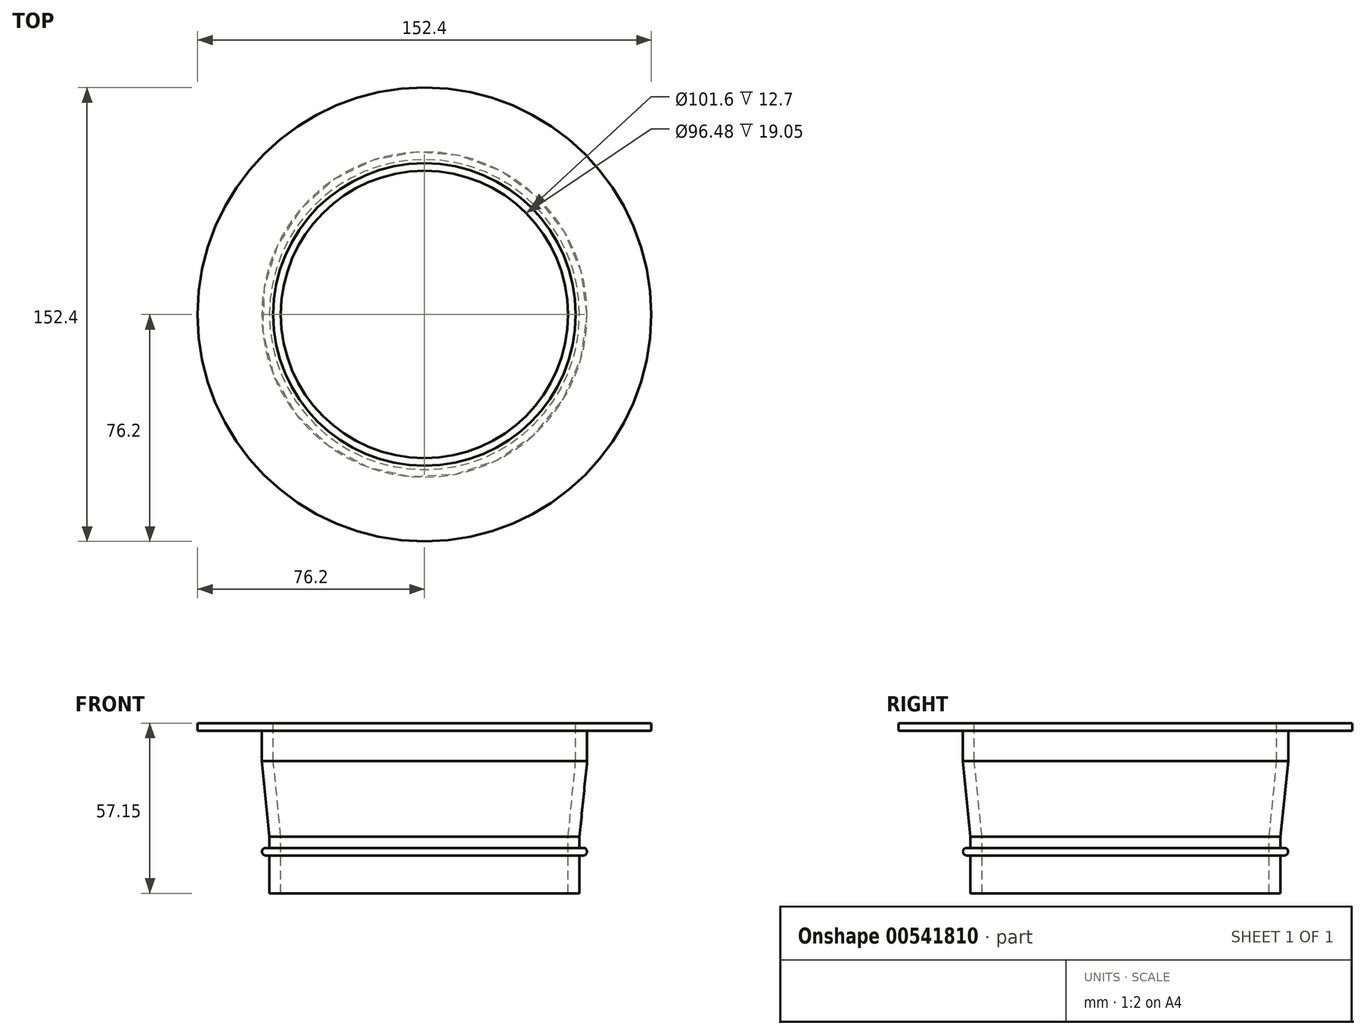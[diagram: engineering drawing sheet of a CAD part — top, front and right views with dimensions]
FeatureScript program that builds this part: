
annotation { "Feature Type Name" : "Feature", "Feature Type Description" : "" }
export const myFeature = defineFeature(function(context is Context, id is Id, definition is map)
    precondition{}
    {
        {
            var Q0;
            Q0=qCreatedBy(makeId("Right.planeOp"),FACE);
            var sketch = newSketch(context, id + "F0", { "sketchPlane" : qUnion([Q0])});
            skLineSegment(sketch, "E0", {"start": v(-48.24, 0) * mm, "end": v(-50.8, 25.4) * mm});
            skLineSegment(sketch, "E1", {"start": v(-52.07, 0) * mm, "end": v(-54.63, 25.4) * mm});
            skLineSegment(sketch, "E2", {"start": v(-54.63, 25.4) * mm, "end": v(-54.63, 38.1) * mm});
            skLineSegment(sketch, "E3", {"start": v(-50.8, 25.4) * mm, "end": v(-50.8, 38.1) * mm});
            skLineSegment(sketch, "E4", {"start": v(-50.8, 38.1) * mm, "end": v(-54.63, 38.1) * mm});
            skLineSegment(sketch, "E5", {"start": v(-48.24, 0) * mm, "end": v(-48.24, -19.05) * mm});
            skLineSegment(sketch, "E6", {"start": v(-52.07, 0) * mm, "end": v(-52.07, -3.81) * mm});
            skLineSegment(sketch, "E7", {"start": v(-48.24, -19.05) * mm, "end": v(-52.07, -19.05) * mm});
            skLineSegment(sketch, "E8", {"start": v(0, 59.15) * mm, "end": v(0, -21.14) * mm});
            skLineSegment(sketch, "E9", {"start": v(-52.07, -3.81) * mm, "end": v(-54.6, -3.81) * mm});
            skLineSegment(sketch, "E10", {"start": v(-54.6, -3.81) * mm, "end": v(-54.6, -6.35) * mm});
            skLineSegment(sketch, "E11", {"start": v(-54.6, -6.35) * mm, "end": v(-52.07, -6.35) * mm});
            skLineSegment(sketch, "E12.trimOffspring", {"start": v(-52.07, -6.35) * mm, "end": v(-52.07, -19.05) * mm});
            skSolve(sketch);
        }
        {
            var Q0;
            Q0=makeQuery(id+"F0.imprint","IMPRINT",FACE,{"disambiguationData":[TD([[makeQuery(id+"F0.imprint","IMPRINT",EDGE,{"derivedFrom":sQuery(id+"F0.wireOp",EDGE,"E0")}),1.0]])]});
            var Q1;
            Q1=sQuery(id+"F0.wireOp",EDGE,"E8");
            revolve(context, id + "F1", {"entities" : qUnion([Q0]), "axis" : qUnion([Q1]), "revolveType" : RevolveType.FULL});
        }
        {
            var Q0;
            Q0=makeQuery(id+"F1.opRevolve","SWEPT_FACE",FACE,{"disambiguationData":[OSD([sQuery(id+"F0.wireOp",EDGE,"E4")])]});
            var sketch = newSketch(context, id + "F2", { "sketchPlane" : qUnion([Q0])});
            skCircle(sketch, "E13", {"center": v(0, 0) * mm, "radius": 76.2 * mm});
            skCircle(sketch, "E14", {"center": v(0, 0) * mm, "radius": 52.1 * mm});
            skSolve(sketch);
        }
        {
            var Q0;
            Q0=makeQuery(id+"F2.imprint","IMPRINT",FACE,{"disambiguationData":[TD([[makeQuery(id+"F2.imprint","IMPRINT",EDGE,{"derivedFrom":sQuery(id+"F2.wireOp",EDGE,"E13")}),1.0]])]});
            var Q1;
            Q1=makeQuery(id+"F2.imprint","IMPRINT",FACE,{"disambiguationData":[TD([[makeQuery(id+"F2.imprint","IMPRINT",EDGE,{"derivedFrom":sQuery(id+"F2.wireOp",EDGE,"E14")}),-1.0]])]});
            extrude(context, id + "F3", {"entities" : qUnion([Q0, Q1]), "operationType" : NewBodyOperationType.ADD, "oppositeDirection" : true, "depth" : 2.54 * mm, "offsetDistance" : 25.4 * mm});
        }
        {
            var Q0;
            Q0=makeQuery(id+"F1.opRevolve","SWEPT_EDGE",EDGE,{"disambiguationData":[OSD([sQuery(id+"F0.wireOp",EDGE,"E9"),sQuery(id+"F0.wireOp",EDGE,"E10")])]});
            var Q1;
            Q1=makeQuery(id+"F1.opRevolve","SWEPT_EDGE",EDGE,{"disambiguationData":[OSD([sQuery(id+"F0.wireOp",EDGE,"E10"),sQuery(id+"F0.wireOp",EDGE,"E11")])]});
            fillet(context, id + "F4", {"entities" : qUnion([Q0, Q1]), "radius" : 1.27 * mm, "tangentPropagation" : true, "allowEdgeOverflow" : false});
        }
    });
